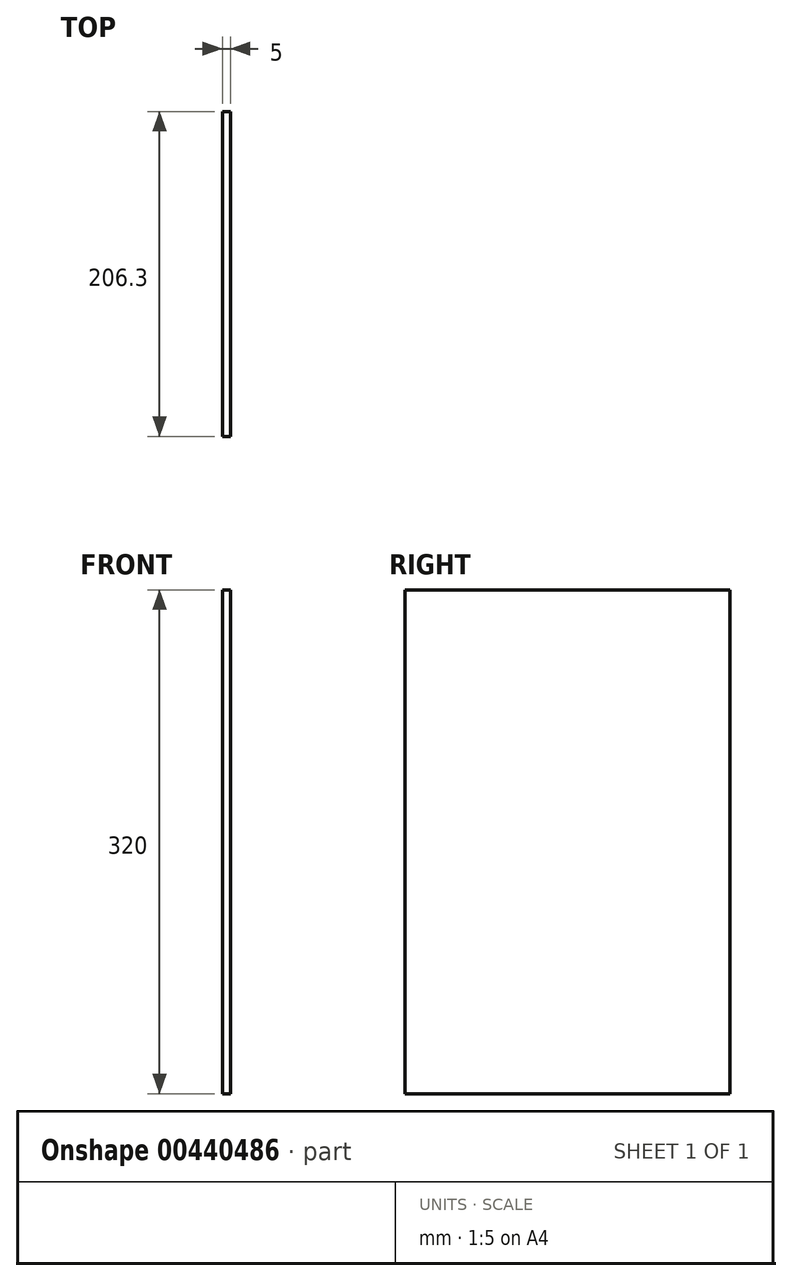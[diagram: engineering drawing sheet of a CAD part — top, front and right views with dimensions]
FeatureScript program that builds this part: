
annotation { "Feature Type Name" : "Feature", "Feature Type Description" : "" }
export const myFeature = defineFeature(function(context is Context, id is Id, definition is map)
    precondition{}
    {
        {
            var Q0;
            Q0=qCreatedBy(makeId("Top.planeOp"),FACE);
            var sketch = newSketch(context, id + "F0", { "sketchPlane" : qUnion([Q0])});
            skLineSegment(sketch, "E0.bottom", {"start": v(2.5, -103.15) * mm, "end": v(-2.5, -103.15) * mm});
            skLineSegment(sketch, "E0.top", {"start": v(2.5, 103.15) * mm, "end": v(-2.5, 103.15) * mm});
            skLineSegment(sketch, "E0.left", {"start": v(2.5, -103.15) * mm, "end": v(2.5, 103.15) * mm});
            skLineSegment(sketch, "E0.right", {"start": v(-2.5, -103.15) * mm, "end": v(-2.5, 103.15) * mm});
            skPoint(sketch, "E0.middle", {"position": v(0, 0) * mm});
            skSolve(sketch);
        }
        {
            var Q0;
            Q0 = qSketchRegion(id + "F0", true);
            extrude(context, id + "F1", {"entities" : qUnion([Q0]), "depth" : 320 * mm, "offsetDistance" : 25 * mm});
        }
    });
